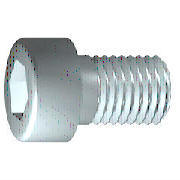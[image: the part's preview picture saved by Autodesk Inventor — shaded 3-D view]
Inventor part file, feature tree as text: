
AUTODESK INVENTOR PART (.ipt)
format: ipt  version: 2019 (Build 230136000, 136)  size: 196,096 bytes
history: native  units: mm (DEFAULTED — no unit token found)
features: sketch x2, extrude x1, plane x1, fillet x1
ambient origin geometry x7: Origin, YZ Plane, XY Plane, X Axis, Y Axis, Z Axis, Center Point
bodies: Solid1 (feature_tree), Body (feature_tree)
feature tree (5):
  extrude  "Slot"  Depth=3.0mm
  plane  "Work Plane1"
  fillet  "Fillet2"  Radius=3.0mm
  sketch  "Sketch1"  dims[d1=12.0mm d2=0.306825mm d3=3.0mm]
  sketch  "Sketch2"  dims[d4=1.3mm d5=60.0deg d6=3.0mm d7=3.0mm d8=2.886751mm d9=5.5mm d10=90.0deg d11=10.0mm d12=0.0mm d13=12.0mm d14=0.0mm d15=0.306725mm d16=0.306725mm d17=0.3mm d19=0.0mm d26=16.0mm d27=45.0deg d28=0.0mm d29=0.0mm d30=0.1mm]
